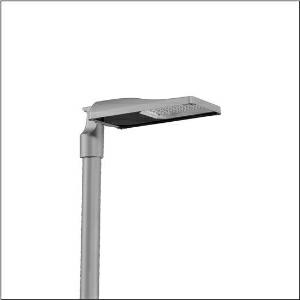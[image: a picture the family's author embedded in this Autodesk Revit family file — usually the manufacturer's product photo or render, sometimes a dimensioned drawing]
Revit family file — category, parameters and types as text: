
# Revit family: streetlight_sl_31_mini___st1_0a_5xh2d31b08ga_4c19
name_source: partatom
category: Lighting Fixtures
units: mm (PartAtom-declared; Revit-internal decimal feet)

## family parameters
Cut with Voids When Loaded = No
Host = Face
Light Source = No
Part Type = Normal
Room Calculation Point = No
Round Connector Dimension = Use Diameter
Shared = No

## types (1)
- --- (1 x LED, 5710 lm, 37.3 W, 3000K)
    Apparent Load = 37 VA
    CIE Flux Codes = 37 72 97 100 100
    Color Rendering = 70
    Color Temperature = 3000K
    Default Elevation = 1800 mm
    Description = Streetlight SL 31 mini Easy, LST, Desk-Remote mast luminaire for post-top, side-entry; light control with lens of PMMA; light distribution: ST1.0a, direct asymmetric distribution, for standard-compliant lighting for roads and squares; LED: luminous flux: 5.710lm, light colour: 730, colour temperature: 3000K; luminous efficacy: 153,1lm/W; control: pre-setting: linear dimming characteristic, flexible luminous flux parameterisation, time-dependent luminous flux control, constant luminous flux control, power reduction, intelligent temperature release in ECG and LED module, overheat protection; luminaire housing, of diecast aluminium, SITECO metallic grey (DB 702S), corrosivity category C5 high according to DIN EN ISO 12944; cover of toughened safety glass, transparent, mast flange of diecast aluminium, SITECO metallic grey (DB 702S), spigot size: 76/60mm, mast flange included unmounted; with cable H07RN-F 5x 1.5mm², cable length: 6,5m, connection cable pre-assembled; mains connection: 220..240V, AC, 50/60Hz; power consumption (at start of service life): 37,3W / (at end of service life): 38,7W / (with reduced operation 50%): 17,5W; protection rating (complete): IP66; insulation class (complete): insulation class II (safety insulation); impact resistance: IK10; certification: CE, ENEC, ENEC+, VDE, UKCA; permissible operating ambient temperature for outdoor applications: -40..+50°C; packaging unit: 1 piece

Light Distribution: ST1.0a
    Height = 76 mm
    Lamp = 1 x LED
    Lamp Light Flux = 5710 lm
    Lamp Power = 37.3 W
    Lamp count = 1
    Length = 547 mm
    Luminous efficacy = 153 lm/W
    Manufacturer = Siteco
    ModVariant = No
    Model = 5XH2D31B08GA
    Number of Poles = 1
    OnlyDefault = Yes
    Power Factor = 1
    Product Name = Streetlight SL 31 mini | ST1.0a
    Product group = mast luminaire | pylon top
    ProductGroupID = 6100
    Protection Class = Protection class II
    Protection Degree = IP 66
    RLX_Detail_Level = 1
    RLX_Emergency_Light_Flux = 0 lm
    RLX_Emergency_Type = 0
    RLX_Emergency_Type_DB = No
    RlxData = <blob elided: 39609 chars, md5=b6896e68>
    Socket = socket
    Standby Power = 0 W
    System Light Flux = 5710 lm
    System Power = 37 W
    Type Comments = factory setting: luminous flux: 100 % | dim-lin: 254 | 386 mA
    Type Image = l_1300326.jpg
    URL = http://relux.com
    VarID = @adj_061729
    Voltage = 0 V
    Weight = 0.00 kg
    Width = 265 mm

## geometry (parser evidence)
native form markers: Blend x4, Sweep x9
no freeform markers — native parametric forms only
